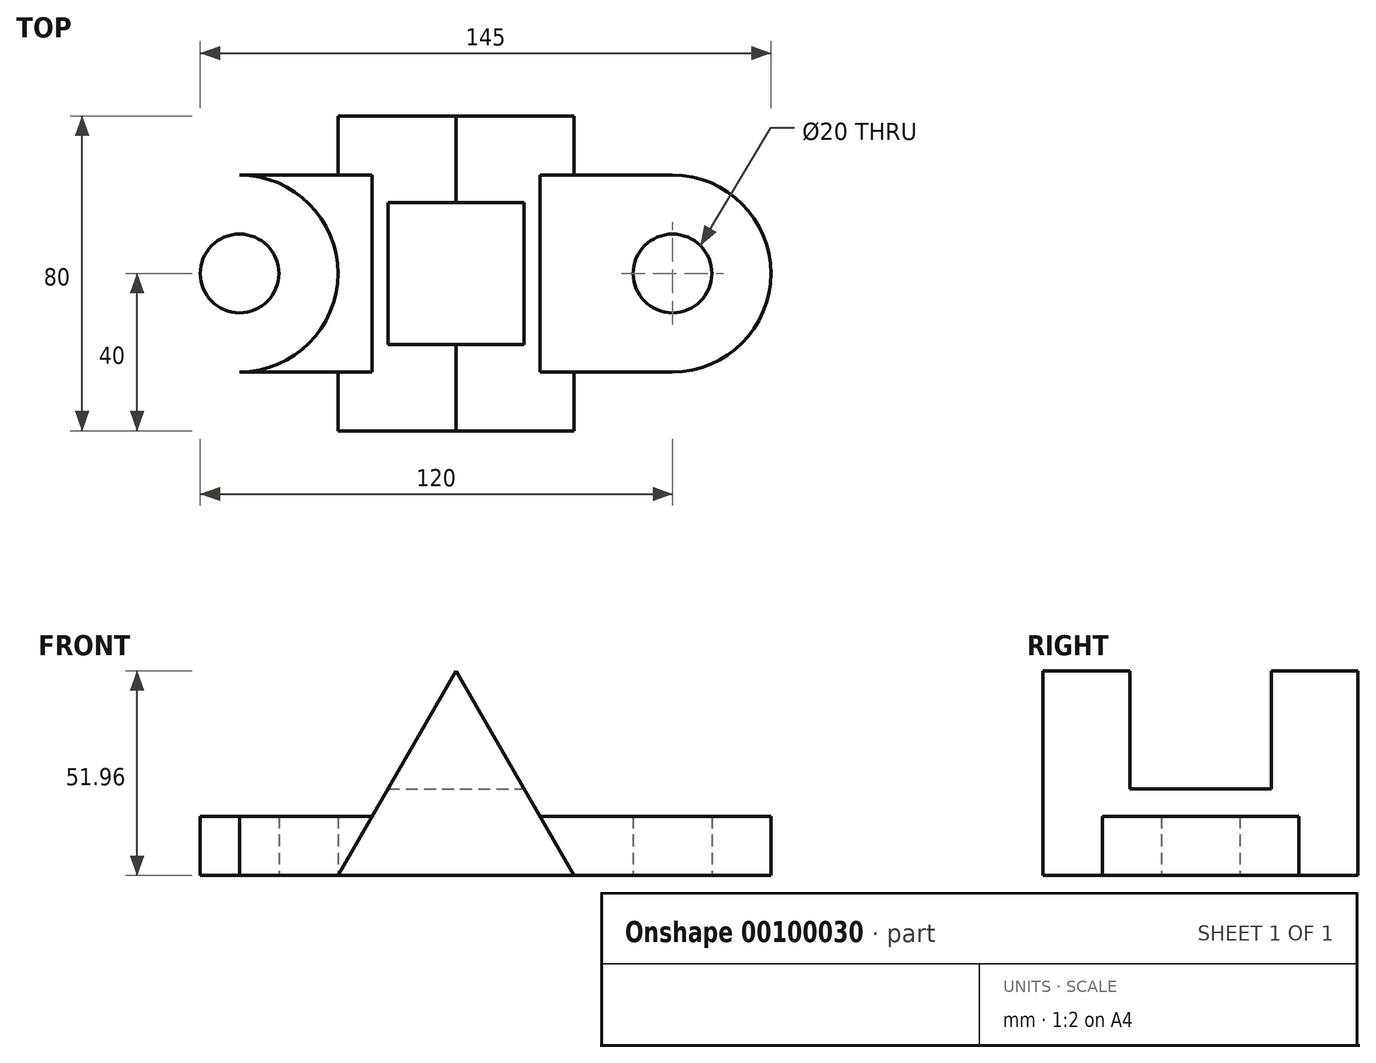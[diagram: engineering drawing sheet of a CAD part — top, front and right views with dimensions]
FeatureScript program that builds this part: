
annotation { "Feature Type Name" : "Feature", "Feature Type Description" : "" }
export const myFeature = defineFeature(function(context is Context, id is Id, definition is map)
    precondition{}
    {
        {
            var Q0;
            Q0=qCreatedBy(makeId("Top.planeOp"),FACE);
            var sketch = newSketch(context, id + "F0", { "sketchPlane" : qUnion([Q0])});
            skCircle(sketch, "E0", {"center": v(55, 0) * mm, "radius": 10 * mm});
            skCircle(sketch, "E1", {"center": v(55, 0) * mm, "radius": 25 * mm});
            skLineSegment(sketch, "E2", {"start": v(55, -25) * mm, "end": v(0, -25) * mm});
            skLineSegment(sketch, "E3", {"start": v(55, 25) * mm, "end": v(0, 25) * mm});
            skCircle(sketch, "E4.MirrorC", {"center": v(-55, 0) * mm, "radius": 10 * mm});
            skCircle(sketch, "E5.MirrorC", {"center": v(-55, 0) * mm, "radius": 25 * mm});
            skLineSegment(sketch, "E6.MirrorCS", {"start": v(-55, -25) * mm, "end": v(0, -25) * mm});
            skLineSegment(sketch, "E7.MirrorCS", {"start": v(-55, 25) * mm, "end": v(0, 25) * mm});
            skLineSegment(sketch, "E8", {"start": v(30, 40) * mm, "end": v(-30, 40) * mm});
            skLineSegment(sketch, "E9", {"start": v(-30, 40) * mm, "end": v(-30, 25) * mm});
            skLineSegment(sketch, "E10", {"start": v(30, 40) * mm, "end": v(30, 25) * mm});
            skLineSegment(sketch, "E11.MirrorCS", {"start": v(30, -40) * mm, "end": v(30, -25) * mm});
            skLineSegment(sketch, "E12.MirrorCS", {"start": v(-30, -40) * mm, "end": v(-30, -25) * mm});
            skLineSegment(sketch, "E13.MirrorCS", {"start": v(30, -40) * mm, "end": v(-30, -40) * mm});
            skSolve(sketch);
        }
        {
            var Q0;
            Q0=qCreatedBy(makeId("Front.planeOp"),FACE);
            var sketch = newSketch(context, id + "F1", { "sketchPlane" : qUnion([Q0])});
            skLineSegment(sketch, "E14", {"start": v(30, 0) * mm, "end": v(-30, 0) * mm});
            skLineSegment(sketch, "E15", {"start": v(-30, 0) * mm, "end": v(0, 51.96) * mm});
            skLineSegment(sketch, "E16", {"start": v(0, 51.96) * mm, "end": v(30, 0) * mm});
            skSolve(sketch);
        }
        {
            var Q0;
            Q0 = qSketchRegion(id + "F1", true);
            extrude(context, id + "F2", {"entities" : qUnion([Q0]), "endBound" : BoundingType.SYMMETRIC, "depth" : 80 * mm});
        }
        {
            var Q0;
            Q0=makeQuery(id+"F0.imprint","IMPRINT",FACE,{"disambiguationData":[TD([[makeQuery(id+"F0.imprint","IMPRINT",EDGE,{"derivedFrom":sQuery(id+"F0.wireOp",EDGE,"E0")}),-1.0]])]});
            var Q1;
            {var subQ1=sQuery(id+"F0.wireOp",EDGE,"E1");var subQ9=sQuery(id+"F0.wireOp",EDGE,"E2");var subQ12=makeQuery(id+"F0.imprint","INTERSECT",VERTEX,{"derivedFrom":[subQ1,subQ9]});Q1=makeQuery(id+"F0.imprint","IMPRINT",FACE,{"disambiguationData":[TD([[makeQuery(id+"F0.imprint","IMPRINT",EDGE,{"disambiguationData":[TD([[subQ12,1.0]])],"derivedFrom":subQ1}),-1.0]])]});}
            var Q2;
            Q2=makeQuery(id+"F0.imprint","IMPRINT",FACE,{"disambiguationData":[TD([[makeQuery(id+"F0.imprint","IMPRINT",EDGE,{"derivedFrom":sQuery(id+"F0.wireOp",EDGE,"E4.MirrorC")}),1.0]])]});
            extrude(context, id + "F3", {"entities" : qUnion([Q0, Q1, Q2]), "operationType" : NewBodyOperationType.ADD, "depth" : 15 * mm});
        }
        {
            var Q0;
            Q0=qCreatedBy(makeId("Right.planeOp"),FACE);
            var sketch = newSketch(context, id + "F4", { "sketchPlane" : qUnion([Q0])});
            skLineSegment(sketch, "E17", {"start": v(-18, 51.96) * mm, "end": v(-18, 21.96) * mm});
            skLineSegment(sketch, "E18", {"start": v(-18, 21.96) * mm, "end": v(18, 21.96) * mm});
            skLineSegment(sketch, "E19", {"start": v(18, 21.96) * mm, "end": v(18, 51.96) * mm});
            skLineSegment(sketch, "E20", {"start": v(-18, 51.96) * mm, "end": v(18, 51.96) * mm});
            skSolve(sketch);
        }
        {
            var Q0;
            Q0 = qSketchRegion(id + "F4", true);
            extrude(context, id + "F5", {"entities" : qUnion([Q0]), "operationType" : NewBodyOperationType.REMOVE, "endBound" : BoundingType.SYMMETRIC, "oppositeDirection" : true, "depth" : 60 * mm});
        }
    });
